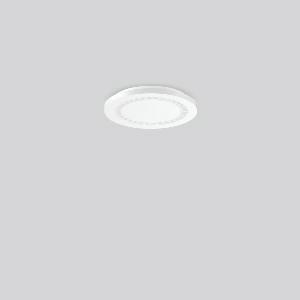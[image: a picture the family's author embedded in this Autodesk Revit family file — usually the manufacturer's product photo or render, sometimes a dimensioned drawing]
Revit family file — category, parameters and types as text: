
# Revit family: hemis_round_312184_002_52f8
name_source: partatom
category: Lighting Fixtures
units: mm (PartAtom-declared; Revit-internal decimal feet)

## family parameters
Cut with Voids When Loaded = No
Host = Face
Light Source = No
Part Type = Normal
Room Calculation Point = No
Round Connector Dimension = Use Diameter
Shared = No

## types (1)
- HEMIS round (1 x LED Modul 830, 1300 lm, 3000)
    Apparent Load = 12 VA
    CIE Flux Codes = 87 99 100 100 100
    Color Rendering = 80
    Color Temperature = 3000
    Default Elevation = 1800 mm
    Description = Series: HEMIS round
Glare-free LED ceiling luminaire with optical lens system. Base: metal, powder-coated, with bayonet fixing. Housing: plastic (polycarbonate). Housing and diffuser are screwed together. Diffuser with optic lenses. Big terminal block; ideal for through-wiring. Sealing strip on the back of the luminaire connects seamlessly with the ceiling. Easy installation with Plug+Play plug connection. Thanks to RUG < 22 ideal for corridors, stairways, shops, schools, meeting rooms, rest areas. 
Colour: white
Diameter: 250 mm
Height: 33 mm
Lamp: LED
Socket: without socket
Colour temperature: 3000K
Colour rendering index (CRI): 80
System power: 12 W
Rated luminous flux: 1300 lm
Luminous efficiency: 108 lm/W
Control gear: Regulated power supply
Protection class: I
Type of protection: IP 40
    Height = 33 mm
    Lamp = 1 x LED Modul 830
    Lamp Light Flux = 1300 lm
    Lamp count = 1
    Length = 250 mm
    Lifetime = 50000 h
    Luminous efficacy = 108 lm/W
    Manufacturer = RZB
    ModVariant = No
    Model = 312184.002
    Mounting Place = Ceiling
    Mounting Type = Surface mounted
    Number of Poles = 1
    OnlyDefault = Yes
    Power Factor = 1
    Product Name = HEMIS round
    Product group = Surface mounted modular luminaires
    ProductGroupID = 306
    Protection Class = Protection class I
    Protection Degree = IP 40
    RLX_Detail_Level = 1
    RLX_Emergency_Light_Flux = 0 lm
    RLX_Emergency_Type = 0
    RLX_Emergency_Type_DB = No
    RlxData = <blob elided: 37345 chars, md5=32c4420e>
    Socket = socket
    Standby Power = 0 W
    System Light Flux = 1300 lm
    System Power = 12 W
    Type Comments = Product without accessories
    Type Image = 312184.002.jpg
    URL = http://relux.com
    VarID = ---
    Voltage = 230 V
    Voltage Range = 220-240 V
    Weight = 0.00 kg
    Width = 0 mm  [stored 0 ft]

note: [stored X ft] marks values corroborated as IEEE doubles in the binary element streams (Revit-internal decimal feet)

## geometry (parser evidence)
native form markers: Blend x4, Sweep x11
no freeform markers — native parametric forms only
